# Revit family: НЕВАТОМ_Узел регулирования SUow3, Версия 2
name_source: partatom
category: Обобщенные модели
revit_build: Autodesk Revit 2017 (Build: 20170118_1100(x64)
units: mm (PartAtom-declared; Revit-internal decimal feet)

## family parameters
Всегда вертикально = Да
Может служить основой для арматурных стержней = Нет
На основе рабочей плоскости = Нет
Общий = Нет
При загрузке вырезать с полостями = Нет
Размер круглого соединителя = Использовать диаметр
Тип детали = Нормальный
Точка расчета площади = Нет

## types (1)
- Узел регулирования SUow3
    ADSK_Единица измерения = шт.
    ADSK_Завод-изготовитель = NEVATOM
    ADSK_Марка = SUow3 10
    ADSK_Наименование = SUow3 10
    ADSK_Расход воздуха = 60.000 м³/ч
    G = 19 мм
    Kvs табличный = 1.6 м³/ч
    L гибкая подводка = 800 мм
    Nevatom_Охладитель расход воды = 2.6 м³/ч
    d = 57 мм
    d гибкой подводки = 20 мм
    f = 0.86
    h1 = 0 мм
    h2 = 0 мм
    h4 = 0 мм
    m = 63 мм
    md = 23 мм
    n = 52 мм
    s = 42 мм
    Ниппель_Габариты = НЕВАТОМ_Ниппель_Габариты
    Тройник_Габариты = НЕВАТОМ_Тройник_Габариты
